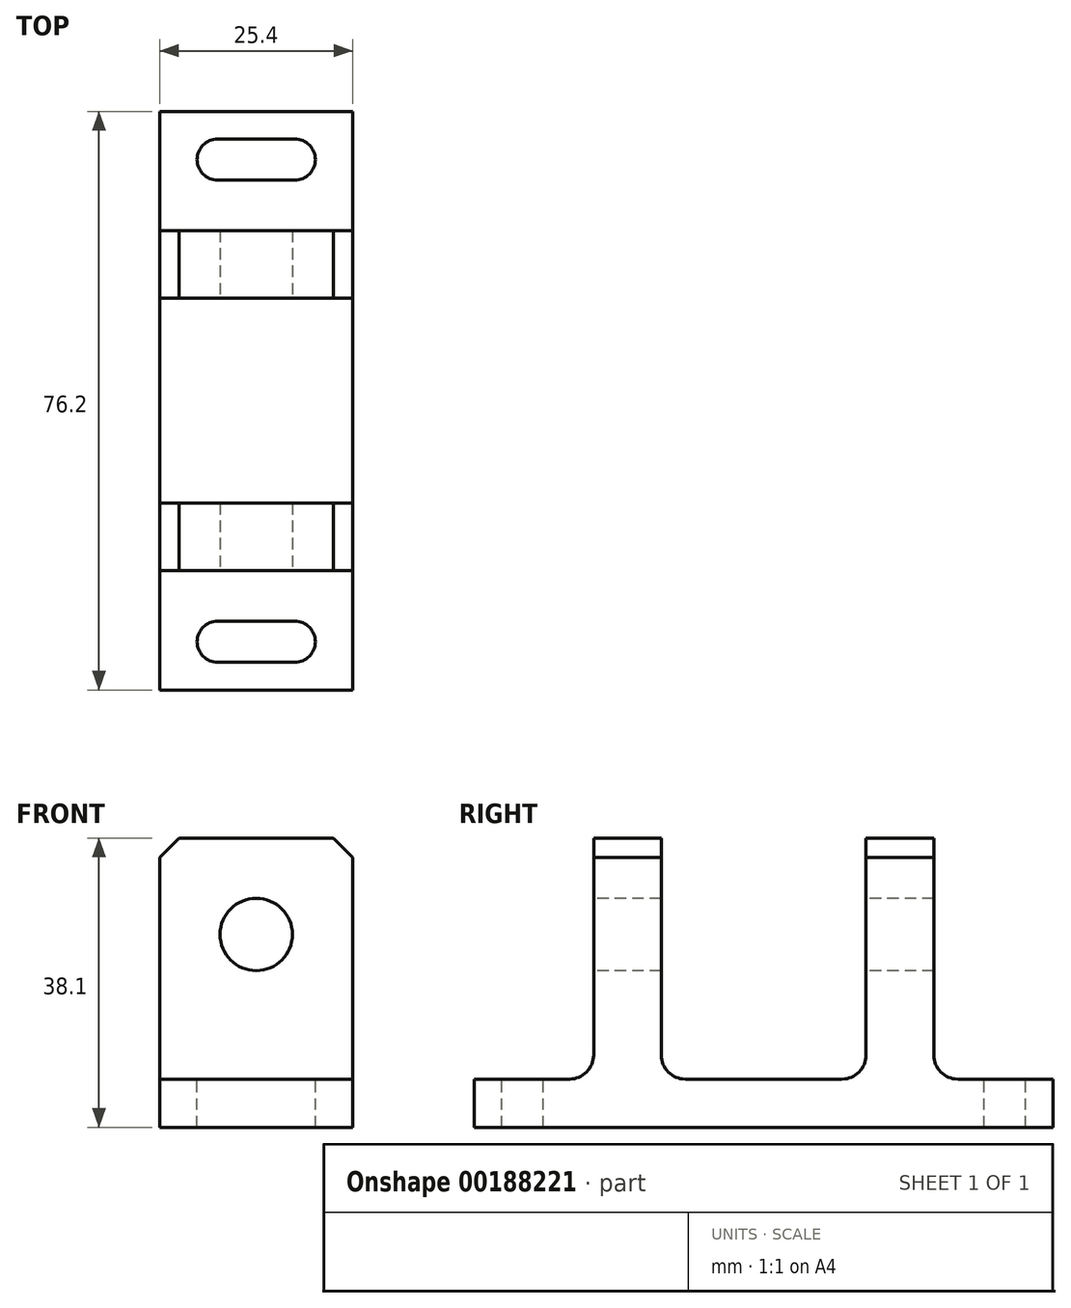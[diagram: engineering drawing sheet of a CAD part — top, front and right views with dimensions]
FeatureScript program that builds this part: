
annotation { "Feature Type Name" : "Feature", "Feature Type Description" : "" }
export const myFeature = defineFeature(function(context is Context, id is Id, definition is map)
    precondition{}
    {
        {
            var Q0;
            Q0=qCreatedBy(makeId("Right.planeOp"),FACE);
            var sketch = newSketch(context, id + "F0", { "sketchPlane" : qUnion([Q0])});
            skLineSegment(sketch, "E0", {"start": v(0, 0) * mm, "end": v(-38.1, 0) * mm});
            skLineSegment(sketch, "E1", {"start": v(-38.1, 0) * mm, "end": v(-38.1, 6.35) * mm});
            skLineSegment(sketch, "E2", {"start": v(-38.1, 6.35) * mm, "end": v(-25.56, 6.35) * mm});
            skLineSegment(sketch, "E3", {"start": v(-22.38, 9.52) * mm, "end": v(-22.38, 38.1) * mm});
            skLineSegment(sketch, "E4", {"start": v(-22.38, 38.1) * mm, "end": v(-13.5, 38.1) * mm});
            skLineSegment(sketch, "E5", {"start": v(-13.5, 38.1) * mm, "end": v(-13.5, 9.52) * mm});
            skLineSegment(sketch, "E6.MirrorCS", {"start": v(22.38, 38.1) * mm, "end": v(13.5, 38.1) * mm});
            skLineSegment(sketch, "E7.MirrorCS", {"start": v(22.38, 9.52) * mm, "end": v(22.38, 38.1) * mm});
            skLineSegment(sketch, "E8.MirrorCS", {"start": v(38.1, 6.35) * mm, "end": v(25.56, 6.35) * mm});
            skLineSegment(sketch, "E9.MirrorCS", {"start": v(38.1, 0) * mm, "end": v(38.1, 6.35) * mm});
            skLineSegment(sketch, "E10.MirrorCS", {"start": v(0, 0) * mm, "end": v(38.1, 0) * mm});
            skLineSegment(sketch, "E11", {"start": v(-10.32, 6.35) * mm, "end": v(0, 6.35) * mm});
            skLineSegment(sketch, "E12.MirrorCS", {"start": v(10.32, 6.35) * mm, "end": v(0, 6.35) * mm});
            skLineSegment(sketch, "E13.MirrorCS", {"start": v(13.5, 38.1) * mm, "end": v(13.5, 9.53) * mm});
            skPoint(sketch, "E14.visualSharp", {"position": v(-22.38, 6.35) * mm});
            skArc(sketch, "E14.filletArc", {"start": v(-25.56, 6.35) * mm, "mid": v(-23.31, 7.28) * mm, "end": v(-22.38, 9.52) * mm});
            skPoint(sketch, "E15.visualSharp", {"position": v(-13.5, 6.35) * mm});
            skArc(sketch, "E15.filletArc", {"start": v(-13.5, 9.52) * mm, "mid": v(-12.56, 7.28) * mm, "end": v(-10.32, 6.35) * mm});
            skPoint(sketch, "E16.visualSharp", {"position": v(13.5, 6.35) * mm});
            skArc(sketch, "E16.filletArc", {"start": v(10.32, 6.35) * mm, "mid": v(12.56, 7.28) * mm, "end": v(13.5, 9.53) * mm});
            skPoint(sketch, "E17.visualSharp", {"position": v(22.38, 6.35) * mm});
            skArc(sketch, "E17.filletArc", {"start": v(22.38, 9.52) * mm, "mid": v(23.31, 7.28) * mm, "end": v(25.56, 6.35) * mm});
            skSolve(sketch);
        }
        {
            var Q0;
            Q0 = qSketchRegion(id + "F0", true);
            extrude(context, id + "F1", {"entities" : qUnion([Q0]), "endBound" : BoundingType.SYMMETRIC, "depth" : 25.4 * mm});
        }
        {
            var Q0;
            Q0=makeQuery(id+"F1.opExtrude","SWEPT_FACE",FACE,{"disambiguationData":[OSD([sQuery(id+"F0.wireOp",EDGE,"E3")])]});
            var sketch = newSketch(context, id + "F2", { "sketchPlane" : qUnion([Q0])});
            skCircle(sketch, "E18", {"center": v(0, 25.4) * mm, "radius": 4.76 * mm});
            skSolve(sketch);
        }
        {
            var Q0;
            Q0 = qSketchRegion(id + "F2", true);
            var Q1;
            Q1=makeQuery(id+"F1.opExtrude","SWEPT_FACE",FACE,{"disambiguationData":[OSD([sQuery(id+"F0.wireOp",EDGE,"E7.MirrorCS")])]});
            extrude(context, id + "F3", {"entities" : qUnion([Q0]), "operationType" : NewBodyOperationType.REMOVE, "endBound" : BoundingType.UP_TO_SURFACE, "oppositeDirection" : true, "endBoundEntityFace" : qUnion([Q1]), "depth" : 25.4 * mm});
        }
        {
            var Q0;
            Q0=makeQuery(id+"F1.opExtrude","SWEPT_FACE",FACE,{"disambiguationData":[OSD([sQuery(id+"F0.wireOp",EDGE,"E8.MirrorCS")])]});
            var sketch = newSketch(context, id + "F4", { "sketchPlane" : qUnion([Q0])});
            skLineSegment(sketch, "E19", {"start": v(-5.08, 31.75) * mm, "end": v(5.08, 31.75) * mm});
            skArc(sketch, "E20.0.startCap", {"start": v(-5.08, 29.05) * mm, "mid": v(-7.78, 31.75) * mm, "end": v(-5.08, 34.45) * mm});
            skArc(sketch, "E20.0.endCap", {"start": v(5.08, 34.45) * mm, "mid": v(7.78, 31.75) * mm, "end": v(5.08, 29.05) * mm});
            skLineSegment(sketch, "E20.0.left", {"start": v(-5.08, 34.45) * mm, "end": v(5.08, 34.45) * mm});
            skLineSegment(sketch, "E20.0.right", {"start": v(-5.08, 29.05) * mm, "end": v(5.08, 29.05) * mm});
            skLineSegment(sketch, "E21.MirrorCS", {"start": v(-5.08, -34.45) * mm, "end": v(5.08, -34.45) * mm});
            skArc(sketch, "E22.MirrorCS", {"start": v(-5.08, -29.05) * mm, "mid": v(-7.78, -31.75) * mm, "end": v(-5.08, -34.45) * mm});
            skLineSegment(sketch, "E23.MirrorCS", {"start": v(-5.08, -29.05) * mm, "end": v(5.08, -29.05) * mm});
            skArc(sketch, "E24.MirrorCS", {"start": v(5.08, -34.45) * mm, "mid": v(7.78, -31.75) * mm, "end": v(5.08, -29.05) * mm});
            skPoint(sketch, "E25", {"position": v(0, 31.75) * mm});
            skPoint(sketch, "E26", {"position": v(0, -31.75) * mm});
            skLineSegment(sketch, "E27", {"start": v(0, -29.05) * mm, "end": v(0, -34.45) * mm});
            skSolve(sketch);
        }
        {
            var Q0;
            Q0 = qSketchRegion(id + "F4", true);
            extrude(context, id + "F5", {"entities" : qUnion([Q0]), "operationType" : NewBodyOperationType.REMOVE, "endBound" : BoundingType.UP_TO_NEXT, "oppositeDirection" : true, "depth" : 25.4 * mm});
        }
        {
            var Q0;
            Q0=makeQuery(id+"F1.opExtrude","CAP_EDGE",EDGE,{"disambiguationData":[OSD([sQuery(id+"F0.wireOp",EDGE,"E4")])],"isStart":false});
            var Q1;
            Q1=makeQuery(id+"F1.opExtrude","CAP_EDGE",EDGE,{"disambiguationData":[OSD([sQuery(id+"F0.wireOp",EDGE,"E6.MirrorCS")])],"isStart":false});
            var Q2;
            Q2=makeQuery(id+"F1.opExtrude","CAP_EDGE",EDGE,{"disambiguationData":[OSD([sQuery(id+"F0.wireOp",EDGE,"E4")])],"isStart":true});
            var Q3;
            Q3=makeQuery(id+"F1.opExtrude","CAP_EDGE",EDGE,{"disambiguationData":[OSD([sQuery(id+"F0.wireOp",EDGE,"E6.MirrorCS")])],"isStart":true});
            chamfer(context, id + "F6", {"entities" : qUnion([Q0, Q1, Q2, Q3]), "width" : 2.54 * mm, "tangentPropagation" : true});
        }
    });
